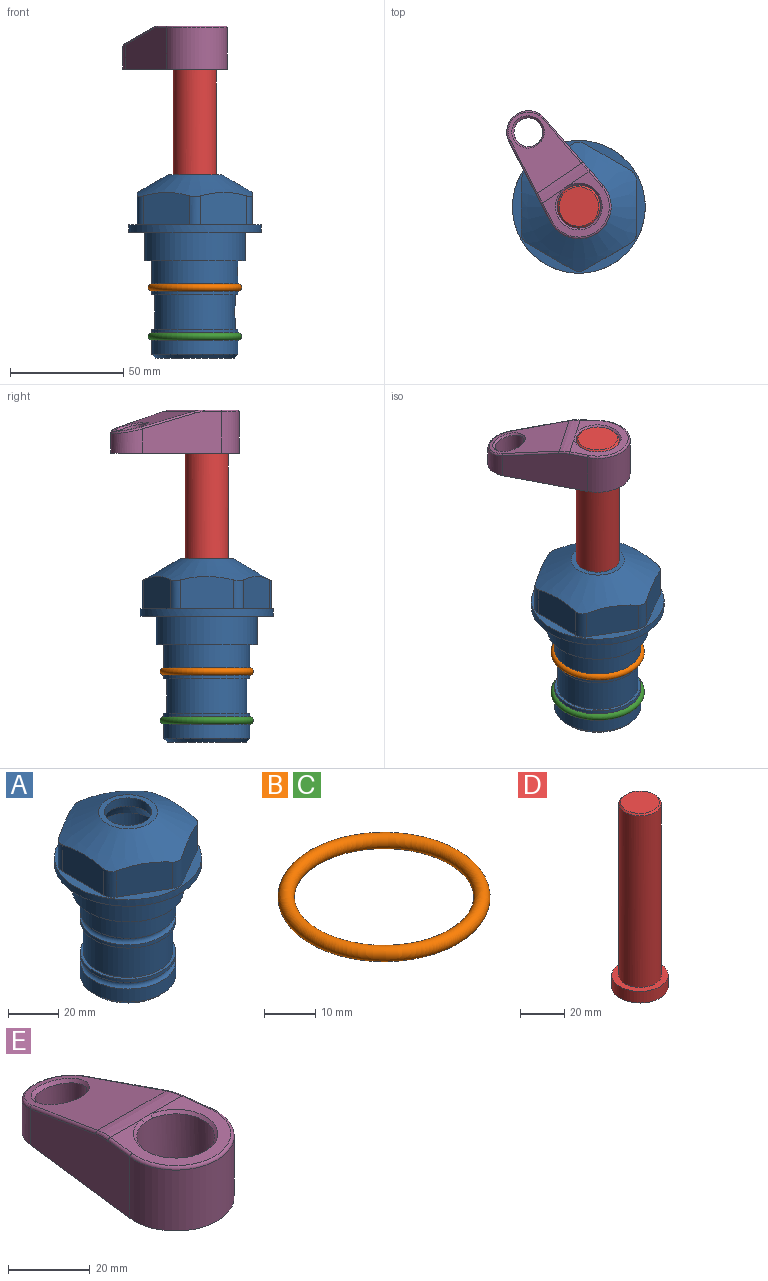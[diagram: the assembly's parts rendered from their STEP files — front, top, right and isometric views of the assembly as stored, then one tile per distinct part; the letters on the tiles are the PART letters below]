
ASSEMBLY  parts=5 mates=4
PART A: 36 faces, bbox 58.7x58.7x81 mm
  f0: cylinder r=17.78mm len=35.56mm, axis (0,0,1), area 1670.8mm2, adj f23,f24,f31
  f1: cylinder r=19.05mm len=38.1mm, axis (0,0,1), area 1191.9mm2, adj f26,f27,f30
  f2: plane 58.66x58.66mm, normal (0,0,-1), area 1150.6mm2, adj f3,f28
  f3: cylinder r=29.33mm len=58.66mm, axis (0,0,-1), area 585.1mm2, adj f2,f4
  f4: plane 58.66x58.66mm, normal (0,0,1), area 475.9mm2, adj f3,f5,f6,f7,f8,f9,f10,f11
  f5: plane 20.32x14.34mm, normal (-0.5,0.87,0), area 324.4mm2, adj f4,f15,f16,f17
  f6: plane 20.32x14.34mm, normal (0.5,0.87,0), area 324.4mm2, adj f4,f14,f15,f17
  f7: plane 23.48x14.34mm, normal (1,0,0), area 324.4mm2, adj f4,f13,f14,f17
  f8: plane 20.32x14.34mm, normal (0.5,-0.87,0), area 324.4mm2, adj f4,f12,f13,f17
  f9: plane 20.32x14.34mm, normal (-0.5,-0.87,0), area 324.4mm2, adj f4,f11,f12,f17
  f10: plane 23.48x14.34mm, normal (-1,0,0), area 324.4mm2, adj f4,f11,f16,f17
  f11: cylinder r=5.08mm len=12.85mm, axis (0,0,-1), area 67.2mm2, adj f4,f9,f10,f17
  f12: cylinder r=5.08mm len=12.85mm, axis (0,0,-1), area 67.2mm2, adj f4,f8,f9,f17
  f13: cylinder r=5.08mm len=12.85mm, axis (0,0,-1), area 67.2mm2, adj f4,f7,f8,f17
  f14: cylinder r=5.08mm len=12.85mm, axis (0,0,-1), area 67.2mm2, adj f4,f6,f7,f17
  f15: cylinder r=5.08mm len=12.85mm, axis (0,0,-1), area 67.2mm2, adj f4,f5,f6,f17
  f16: cylinder r=5.08mm len=12.85mm, axis (0,0,-1), area 67.2mm2, adj f4,f5,f10,f17
  f17: cone r=11.73mm half-angle=60deg, axis (0,0,-1), area 2071.8mm2, adj f5,f6,f7,f8,f9,f10,f11,f12
  f18: plane 23.46x23.46mm, normal (0,0,1), area 147.4mm2, adj f17,f35
  f19: plane 34.93x34.93mm, normal (0,0,-1), area 958mm2, adj f29
  f20: cylinder r=19.05mm len=38.1mm, axis (0,0,1), area 760.1mm2, adj f21,f29
  f21: torus R=19.05mm, axis (0,0,1), area 565.3mm2, adj f20,f22
  f22: cylinder r=19.05mm len=38.1mm, axis (0,0,1), area 190mm2, adj f21,f23
  f23: plane 38.1x38.1mm, normal (0,0,1), area 146.9mm2, adj f0,f22
  f24: plane 38.1x38.1mm, normal (0,0,-1), area 146.9mm2, adj f0,f25
  f25: cylinder r=19.05mm len=38.1mm, axis (0,0,1), area 190mm2, adj f24,f26
  f26: torus R=19.05mm, axis (0,0,1), area 565.3mm2, adj f1,f25
  f27: plane 44.45x44.45mm, normal (0,0,-1), area 411.7mm2, adj f1,f28
  f28: cylinder r=22.23mm len=44.45mm, axis (0,0,1), area 1773.5mm2, adj f2,f27
  f29: cone r=19.05mm half-angle=45deg, axis (0,0,1), area 257.5mm2, adj f19,f20
  f30: cylinder r=3.17mm len=6.75mm, axis (-1,0,0), area 128mm2, adj f1,f33
  f31: cylinder r=3.17mm len=6.35mm, axis (-1,0,0), area 102.5mm2, adj f0,f33
  f32: plane 25.4x25.4mm, normal (0,0,1), area 506.7mm2, adj f33
  f33: cylinder r=12.7mm len=66.42mm, axis (0,0,-1), area 5236.2mm2, adj f30,f31,f32,f34
  f34: cone r=9.53mm half-angle=30deg, axis (0,0,-1), area 443.4mm2, adj f33,f35
  f35: cylinder r=9.53mm len=19.05mm, axis (0,0,-1), area 240.9mm2, adj f18,f34
PART B: 1 faces, bbox 44.7x44.7x3.2 mm
  f0: torus R=19.05mm, axis (0,0,1), area 1193.9mm2
PART C: same geometry as B
PART D: 6 faces, bbox 25.4x25.4x101.6 mm
  f0: plane 17.46x17.46mm, normal (0,0,1), area 239.5mm2, adj f5
  f1: plane 25.4x25.4mm, normal (0,0,-1), area 506.7mm2, adj f2
  f2: cylinder r=12.7mm len=25.4mm, axis (0,0,1), area 506.7mm2, adj f1,f3
  f3: plane 25.4x25.4mm, normal (0,0,1), area 221.7mm2, adj f2,f4
  f4: cylinder r=9.53mm len=94.46mm, axis (0,0,1), area 5653mm2, adj f3,f5
  f5: cone r=8.73mm half-angle=45deg, axis (0,0,-1), area 64.4mm2, adj f0,f4
PART E: 31 faces, bbox 31.7x65.5x19.8 mm
  f0: plane 39.12x18.26mm, normal (0.99,0.12,0), area 612.2mm2, adj f1,f4,f7,f11,f13,f15
  f1: cylinder r=9.53mm len=18.91mm, axis (0,0,-1), area 296.1mm2, adj f0,f2,f7,f17
  f2: plane 39.12x18.26mm, normal (-0.99,0.12,0), area 612.2mm2, adj f1,f4,f7,f12,f14,f16
  f3: cylinder r=6.35mm len=12.7mm, axis (0,0,-1), area 362.4mm2, adj f7,f18
  f4: cylinder r=14.29mm len=28.58mm, axis (0,0,-1), area 882.2mm2, adj f0,f2,f7,f10
  f5: cylinder r=9.53mm len=19.05mm, axis (0,0,-1), area 1092.6mm2, adj f7,f19,f20
  f6: plane 26.99x23.69mm, normal (0,0,1), area 216.2mm2, adj f9,f10,f11,f12,f19
  f7: plane 63.5x28.58mm, normal (0,0,-1), area 661.8mm2, adj f0,f1,f2,f3,f4,f5,f22,f23
  f8: plane 33.52x23.6mm, normal (0,0.26,0.97), area 486mm2, adj f9,f15,f16,f17,f18
  f9: cylinder r=19.05mm len=24.72mm, axis (1,0,0), area 120.4mm2, adj f6,f8,f13,f14,f20
  f10: torus R=13.49mm, axis (0,0,1), area 59mm2, adj f4,f6,f11,f12
  f11: cylinder r=0.79mm len=8.67mm, axis (0.12,-0.99,0), area 10.8mm2, adj f0,f6,f10,f13
  f12: cylinder r=0.79mm len=8.67mm, axis (0.12,0.99,0), area 10.8mm2, adj f2,f6,f10,f14
  f13: bspline ~4.95x1.42mm, area 6.1mm2, adj f0,f9,f11,f15
  f14: bspline ~4.95x1.42mm, area 6.1mm2, adj f2,f9,f12,f16
  f15: cylinder r=0.79mm len=25.95mm, axis (0.12,-0.96,0.26), area 32.9mm2, adj f0,f8,f13,f17
  f16: cylinder r=0.79mm len=25.95mm, axis (0.12,0.96,-0.26), area 32.9mm2, adj f2,f8,f14,f17
  f17: bspline ~18.91x8.38mm, area 30mm2, adj f1,f8,f15,f16
  f18: bspline ~14.29x14.29mm, area 48.3mm2, adj f3,f8
  f19: cone r=9.53mm half-angle=45deg, axis (0,0,1), area 66.5mm2, adj f5,f6,f20
  f20: bspline ~3.22x0.96mm, area 3.5mm2, adj f5,f9,f19
  f21: plane 2.75x2.72mm, normal (0,0,-1), area 2.9mm2, adj f23,f25,f28
  f22: plane 23.05x15.88mm, normal (-0.99,-0.12,0), area 323.6mm2, adj f7,f25,f26,f27,f28,f29
  f23: plane 23.05x15.88mm, normal (0.99,-0.12,0), area 323.6mm2, adj f7,f21,f25,f27,f28,f30
  f24: cylinder r=9.53mm len=10.69mm, axis (0,0,-1), area 114.7mm2, adj f7,f27,f29,f30
  f25: cylinder r=12.7mm len=20.59mm, axis (0,0,-1), area 381.1mm2, adj f7,f21,f22,f23,f26,f28
  f26: plane 2.75x2.72mm, normal (0,0,-1), area 2.9mm2, adj f22,f25,f28
  f27: plane 19.72x18.37mm, normal (0,-0.26,-0.97), area 291.8mm2, adj f22,f23,f24,f28,f29,f30
  f28: cylinder r=15.88mm len=19.92mm, axis (1,0,0), area 54.8mm2, adj f21,f22,f23,f25,f26,f27
  f29: cylinder r=1.59mm len=11mm, axis (0,0,-1), area 34.7mm2, adj f7,f22,f24,f27
  f30: cylinder r=1.59mm len=11mm, axis (0,0,-1), area 34.7mm2, adj f7,f23,f24,f27
PLACE A at identity fixed
PLACE B at identity
PLACE C t=(0,0,-21.59)mm
PLACE D rot(axis=(0,0,1),34.2deg) t=(0,0,27.55)mm
PLACE E rot(axis=(0,0,1),34.2deg) t=(0,0,27.55)mm
MATE cylindrical D.f2 <-> A.f0  axis (0,0,-1) through (0,0,-10.55)mm
MATE fastened A.f0 <-> C.f0  axis (0,0,1) through (0,0,-46.1)mm
MATE fastened E.f4 <-> D.f2  axis (0,0,1) through (0,0,91.05)mm
MATE fastened A.f0 <-> B.f0  axis (0,0,1) through (0,0,-24.51)mm
